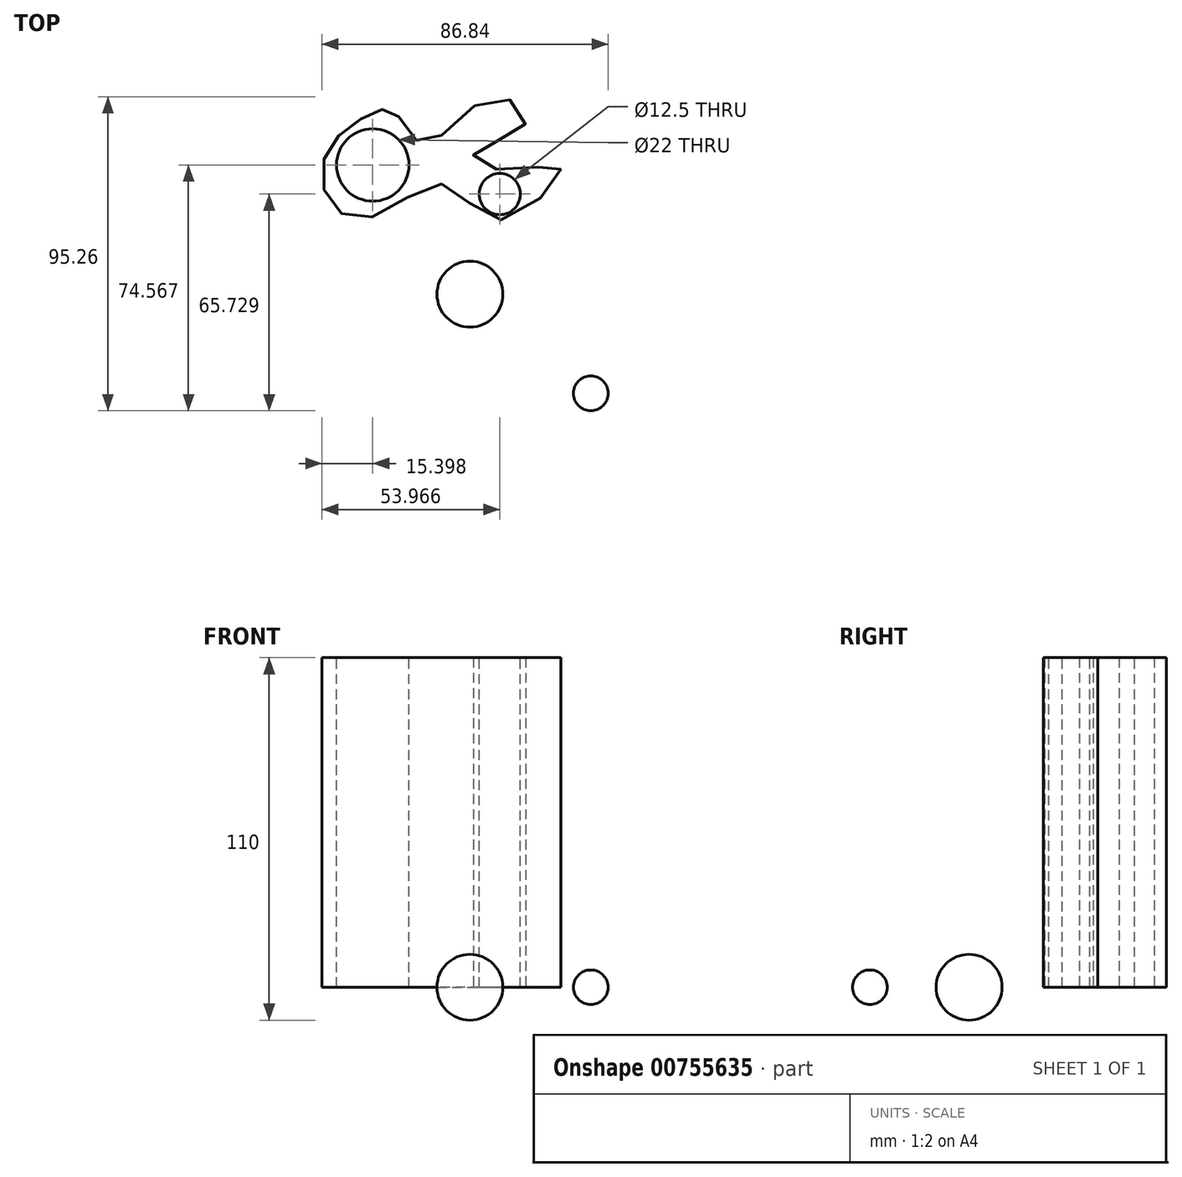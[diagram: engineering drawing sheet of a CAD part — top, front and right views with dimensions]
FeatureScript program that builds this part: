
annotation { "Feature Type Name" : "Feature", "Feature Type Description" : "" }
export const myFeature = defineFeature(function(context is Context, id is Id, definition is map)
    precondition{}
    {
        {
            var Q0;
            Q0=qCreatedBy(makeId("Right.planeOp"),FACE);
            var sketch = newSketch(context, id + "F0", { "sketchPlane" : qUnion([Q0])});
            skArc(sketch, "E0", {"start": v(0, 10) * mm, "mid": v(-10, 0) * mm, "end": v(0, -10) * mm});
            skLineSegment(sketch, "E1", {"start": v(0, 31.55) * mm, "end": v(0, -18.67) * mm, "construction": true});
            skLineSegment(sketch, "E2", {"start": v(0, 10) * mm, "end": v(0, -10) * mm});
            skSolve(sketch);
        }
        {
            var Q0;
            Q0 = qSketchRegion(id + "F0", true);
            var Q1;
            Q1=sQuery(id+"F0.wireOp",EDGE,"E1");
            revolve(context, id + "F1", {"surfaceOperationType" : NewSurfaceOperationType.NEW, "entities" : qUnion([Q0]), "axis" : qUnion([Q1]), "revolveType" : RevolveType.FULL});
        }
        {
            var Q0;
            Q0=qCreatedBy(makeId("Top.planeOp"),FACE);
            var sketch = newSketch(context, id + "F2", { "sketchPlane" : qUnion([Q0])});
            skFitSpline(sketch, "E3", {"points": [v(-29.73, 23.4) * mm, v(-7.98, 33.38) * mm, v(9.18, 22.58) * mm, v(27.52, 38.1) * mm, v(10.66, 37.64) * mm, v(1.23, 43.06) * mm, v(16.69, 51.36) * mm, v(7.37, 59.87) * mm, v(-13.39, 45.58) * mm, v(-21.91, 54.27) * mm, v(-26.64, 56.06) * mm, v(-35.57, 51.51) * mm, v(-43.82, 42.42) * mm, v(-42.64, 28.1) * mm, v(-29.73, 23.4) * mm]});
            skSolve(sketch);
        }
        {
            var Q0;
            Q0 = qSketchRegion(id + "F2", true);
            extrude(context, id + "F3", {"entities" : qUnion([Q0]), "depth" : 100 * mm, "offsetDistance" : 25 * mm});
        }
        {
            var Q0;
            Q0=makeQuery(id+"F3.opExtrude","CAP_FACE",FACE,{"disambiguationData":[OSD([sQuery(id+"F2.wireOp",EDGE,"E3")])],"isStart":false});
            var sketch = newSketch(context, id + "F4", { "sketchPlane" : qUnion([Q0])});
            skCircle(sketch, "E4", {"center": v(-29.5, 39.23) * mm, "radius": 11 * mm});
            skCircle(sketch, "E5", {"center": v(9.07, 30.39) * mm, "radius": 6.25 * mm});
            skSolve(sketch);
        }
        {
            var Q0;
            Q0 = qSketchRegion(id + "F4", true);
            extrude(context, id + "F5", {"entities" : qUnion([Q0]), "operationType" : NewBodyOperationType.REMOVE, "oppositeDirection" : true, "depth" : 100 * mm, "offsetDistance" : 25 * mm});
        }
        {
            var Q0;
            Q0=qCreatedBy(makeId("Top.planeOp"),FACE);
            var sketch = newSketch(context, id + "F6", { "sketchPlane" : qUnion([Q0])});
            skLineSegment(sketch, "E6", {"start": v(36.69, -56.81) * mm, "end": v(36.69, -7.2) * mm, "construction": true});
            skPoint(sketch, "E7", {"position": v(36.69, -30.09) * mm});
            skArc(sketch, "E8", {"start": v(36.69, -24.84) * mm, "mid": v(31.44, -30.09) * mm, "end": v(36.69, -35.34) * mm});
            skLineSegment(sketch, "E9", {"start": v(36.69, -35.34) * mm, "end": v(36.69, -24.84) * mm});
            skSolve(sketch);
        }
        {
            var Q0;
            Q0 = qSketchRegion(id + "F6", true);
            var Q1;
            Q1=sQuery(id+"F6.wireOp",EDGE,"E6");
            revolve(context, id + "F7", {"surfaceOperationType" : NewSurfaceOperationType.NEW, "entities" : qUnion([Q0]), "axis" : qUnion([Q1]), "revolveType" : RevolveType.FULL});
        }
    });
